# Revit family: Bleacher-Telescopic-Hussey-MAXAM_Plus-Portable_with_Aisle-Simplified
name_source: partatom
category: Specialty Equipment
units: mm (PartAtom-declared; Revit-internal decimal feet)

## family parameters
Always vertical = Yes
Cut with Voids When Loaded = No
Enable Cutting in Views = No
Maintain Annotation Orientation = No
OmniClass Number = 23.40.50.34.14
OmniClass Title = Gymnasium Equipment
Part Type = Normal
Room Calculation Point = No
Round Connector Dimension = Use Diameter
Shared = No
Work Plane-Based = No

## types (1)
- 32" Row, 11 5/8" Rise
    16" Row Rise Note = Not Available for Portable Units
    Aisle Step Material = Hussey - Bleacher Step
    Assembly Code = E1020900
    BIM Version = v3.1
    Bank Length Increment = 18'' Typical Increments
    Bank Length Maximum = 19'-5''
    Bank Length Minimum = 10'-6''
    Bleacher Deck Material = Hussey - Plywood - 001 Natural - Bleacher Decking
    CSI MasterFormat = 12 66 00
    Default Elevation = 0"
    Description = MAXAM Plus Telescopic Gym Bleacher Bank and One Aisle - Portable
    End Rail Color = Hussey - Bleacher Rail Color
    Flex Row Note = Not part of Revit Family - Contact Hussey Seating Co.
    Front Closure Material = Hussey - Galvanized Steel
    Handrail Color = Hussey - Bleacher Rail Color
    Manufacturer = Hussey Seating Company
    Metro Chair = Yes
    Metro Chair Arms Note = Not Available with 18'' Width
    Metro Chair Standard Widths = 18'', 19'', 20'', 21'', 22''
    Model = MAXAM Plus
    Nose Beam Material = Hussey - Galvanized Steel
    Not Metro Chair = No
    Optional Rear Panel = Yes
    Product Page URL = http://www.husseyseating.com
    Rear Panel Material = Hussey - Plywood - 001 Natural - Rear Panel
    Riser Material = Hussey - Galvanized Steel
    Row Rise = 11 5/8"
    Row Rise Constraint = 2
    Row Rise Note = Do Not Change Row Rise Constraint
    Row Spacing = 2' - 8"
    Row Spacing Constraint = 2
    Row Spacing Note = Do Not Change Row Spacing Constraint
    Scheduled Seat Width = 1' - 9"
    Seat Type = Bleacher Seat : Metro Chair
    Seat Width = 1' - 9"
    Stanchion Color = Hussey - 301 Blue
    Type Comments = Bleacher Bank and One Aisle
    URL = http://www.husseyseating.com

## geometry (parser evidence)
native form markers: Blend x38, Extrusion x10, Sweep x64
no freeform markers — native parametric forms only
